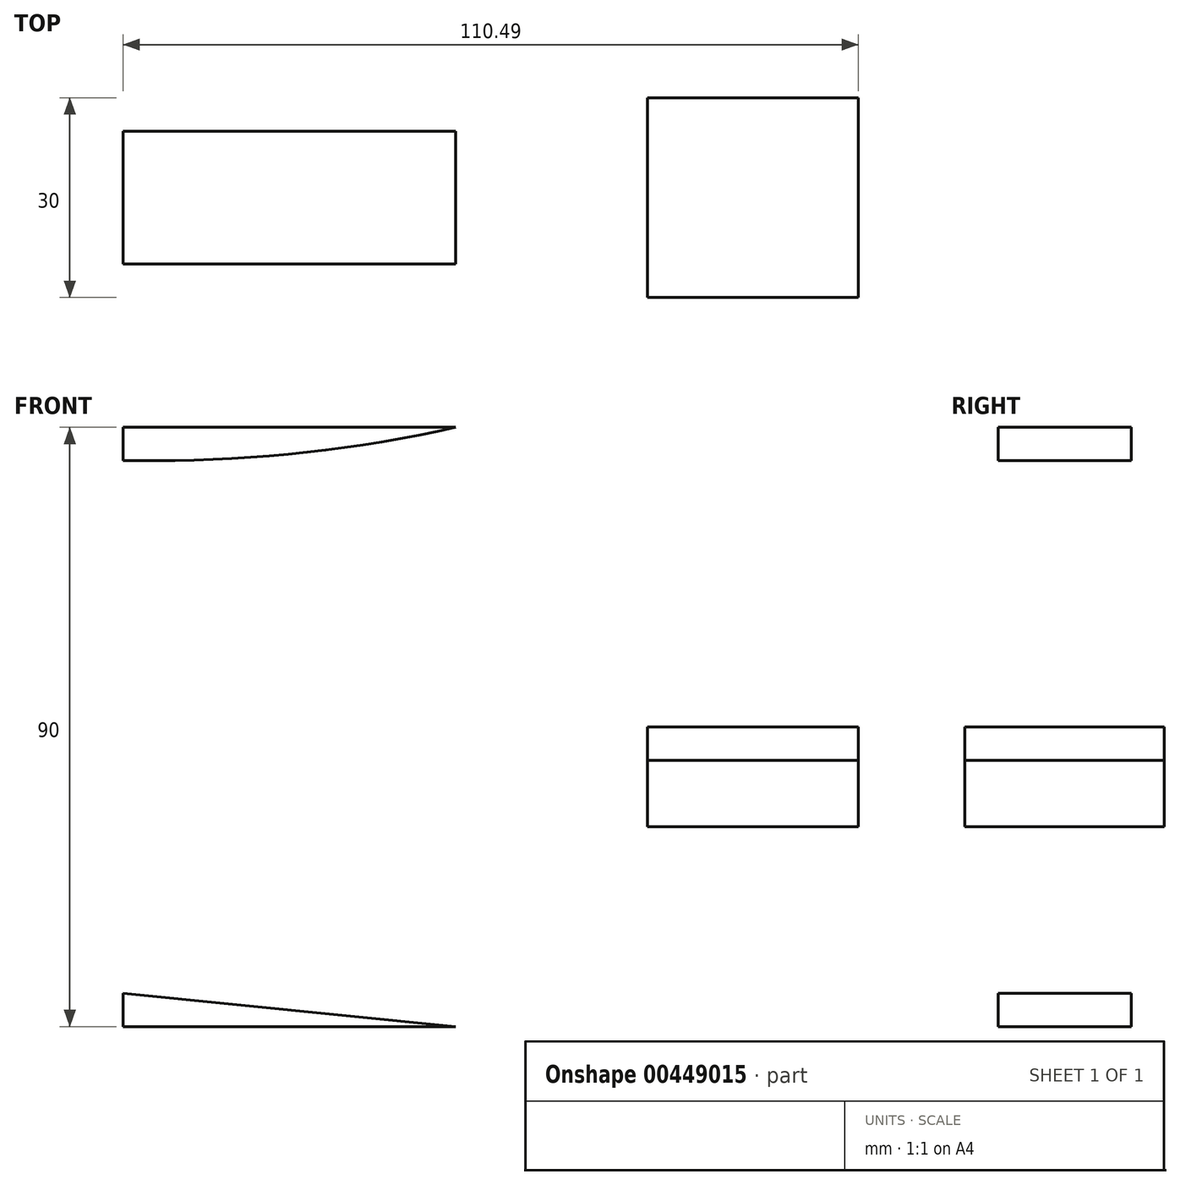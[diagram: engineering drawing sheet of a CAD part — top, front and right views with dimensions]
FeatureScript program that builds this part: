
annotation { "Feature Type Name" : "Feature", "Feature Type Description" : "" }
export const myFeature = defineFeature(function(context is Context, id is Id, definition is map)
    precondition{}
    {
        {
            var Q0;
            Q0=qCreatedBy(makeId("Front.planeOp"),FACE);
            var sketch = newSketch(context, id + "F0", { "sketchPlane" : qUnion([Q0])});
            skLineSegment(sketch, "E0.bottom", {"start": v(69.59, 0) * mm, "end": v(119.59, 0) * mm});
            skLineSegment(sketch, "E0.top", {"start": v(69.59, 5) * mm, "end": v(119.59, 5) * mm});
            skLineSegment(sketch, "E0.left", {"start": v(69.59, 0) * mm, "end": v(69.59, 5) * mm});
            skLineSegment(sketch, "E0.right", {"start": v(119.59, 0) * mm, "end": v(119.59, 5) * mm});
            skLineSegment(sketch, "E1.bottom", {"start": v(69.59, 5) * mm, "end": v(74.59, 5) * mm});
            skLineSegment(sketch, "E1.top", {"start": v(69.59, 55) * mm, "end": v(74.59, 55) * mm});
            skLineSegment(sketch, "E1.left", {"start": v(69.59, 5) * mm, "end": v(69.59, 55) * mm});
            skLineSegment(sketch, "E1.right", {"start": v(74.59, 5) * mm, "end": v(74.59, 55) * mm});
            skLineSegment(sketch, "E2.bottom", {"start": v(69.59, 55) * mm, "end": v(119.59, 55) * mm});
            skLineSegment(sketch, "E2.top", {"start": v(69.59, 60) * mm, "end": v(119.59, 60) * mm});
            skLineSegment(sketch, "E2.left", {"start": v(69.59, 55) * mm, "end": v(69.59, 60) * mm});
            skLineSegment(sketch, "E2.right", {"start": v(119.59, 55) * mm, "end": v(119.59, 60) * mm});
            skLineSegment(sketch, "E3.MirrorCS", {"start": v(69.59, -5) * mm, "end": v(119.59, -5) * mm});
            skLineSegment(sketch, "E4", {"start": v(69.59, -5) * mm, "end": v(69.59, 0) * mm});
            skLineSegment(sketch, "E5", {"start": v(119.59, -5) * mm, "end": v(119.59, 0) * mm});
            skArc(sketch, "E6", {"start": v(74.59, 55) * mm, "mid": v(97.22, 56.25) * mm, "end": v(119.59, 60) * mm});
            skLineSegment(sketch, "E7.bottom", {"start": v(119.59, -25) * mm, "end": v(69.59, -25) * mm});
            skLineSegment(sketch, "E7.top", {"start": v(119.59, -30) * mm, "end": v(69.59, -30) * mm});
            skLineSegment(sketch, "E7.left", {"start": v(119.59, -25) * mm, "end": v(119.59, -30) * mm});
            skLineSegment(sketch, "E7.right", {"start": v(69.59, -25) * mm, "end": v(69.59, -30) * mm});
            skLineSegment(sketch, "E8", {"start": v(69.59, -25) * mm, "end": v(119.59, -30) * mm});
            skSolve(sketch);
        }
        {
            var Q0;
            Q0=makeQuery(id+"F0.imprint","IMPRINT",FACE,{"disambiguationData":[TD([[makeQuery(id+"F0.imprint","IMPRINT",EDGE,{"derivedFrom":sQuery(id+"F0.wireOp",EDGE,"E2.top")}),-1.0]])]});
            var Q1;
            {var subQ0=sQuery(id+"F0.wireOp",EDGE,"d88ff40e-2887-472f-8713-1230f44090761.MirrorCS");Q1=makeQuery(id+"F0.imprint","IMPRINT",FACE,{"disambiguationData":[TD([[makeQuery(id+"F0.imprint","IMPRINT",EDGE,{"derivedFrom":subQ0}),1.0]])]});}
            var Q2;
            Q2=makeQuery(id+"F0.imprint","IMPRINT",FACE,{"disambiguationData":[TD([[makeQuery(id+"F0.imprint","IMPRINT",EDGE,{"derivedFrom":sQuery(id+"F0.wireOp",EDGE,"E7.top")}),-1.0]])]});
            extrude(context, id + "F1", {"entities" : qUnion([Q0, Q1, Q2]), "endBound" : BoundingType.SYMMETRIC, "oppositeDirection" : true, "depth" : 20 * mm});
        }
        {
            var Q0;
            Q0=qCreatedBy(makeId("Top.planeOp"),FACE);
            var sketch = newSketch(context, id + "F2", { "sketchPlane" : qUnion([Q0])});
            skLineSegment(sketch, "E9.bottom", {"start": v(148.37, 15) * mm, "end": v(180.08, 15) * mm});
            skLineSegment(sketch, "E9.top", {"start": v(148.37, -15) * mm, "end": v(180.08, -15) * mm});
            skLineSegment(sketch, "E9.left", {"start": v(148.37, 15) * mm, "end": v(148.37, -15) * mm});
            skLineSegment(sketch, "E9.right", {"start": v(180.08, 15) * mm, "end": v(180.08, -15) * mm});
            skPoint(sketch, "E9.middle", {"position": v(164.22, 0) * mm});
            skSolve(sketch);
        }
        {
            var Q0;
            Q0=makeQuery(id+"F2.imprint","IMPRINT",FACE,{"disambiguationData":[TD([[makeQuery(id+"F2.imprint","IMPRINT",EDGE,{"derivedFrom":sQuery(id+"F2.wireOp",EDGE,"E9.bottom")}),-1.0]])]});
            extrude(context, id + "F3", {"entities" : qUnion([Q0]), "depth" : 10 * mm});
        }
        {
            var Q0;
            Q0=makeQuery(id+"F3.opExtrude","CAP_FACE",FACE,{"disambiguationData":[OSD([sQuery(id+"F2.wireOp",EDGE,"E9.bottom"),sQuery(id+"F2.wireOp",EDGE,"E9.top"),sQuery(id+"F2.wireOp",EDGE,"E9.left"),sQuery(id+"F2.wireOp",EDGE,"E9.right")])],"isStart":false});
            extrude(context, id + "F4", {"entities" : qUnion([Q0]), "depth" : 5 * mm});
        }
    });
